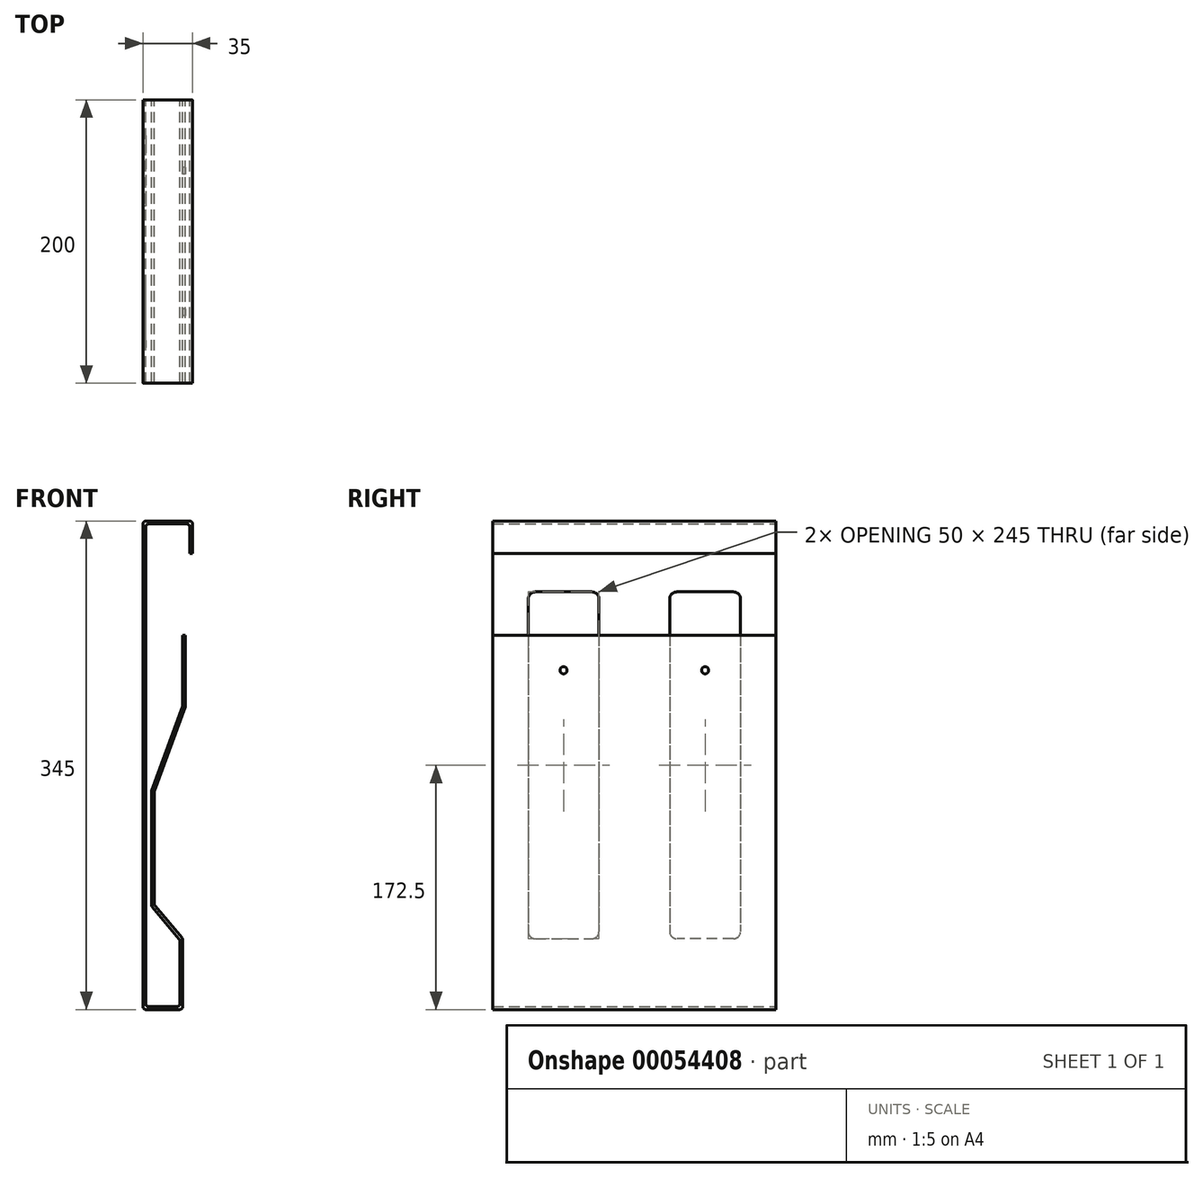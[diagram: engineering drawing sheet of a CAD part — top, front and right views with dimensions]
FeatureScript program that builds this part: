
annotation { "Feature Type Name" : "Feature", "Feature Type Description" : "" }
export const myFeature = defineFeature(function(context is Context, id is Id, definition is map)
    precondition{}
    {
        {
            var Q0;
            Q0=qCreatedBy(makeId("Front.planeOp"),FACE);
            var sketch = newSketch(context, id + "F0", { "sketchPlane" : qUnion([Q0])});
            skLineSegment(sketch, "E0", {"start": v(0, 0) * mm, "end": v(35, 0) * mm});
            skLineSegment(sketch, "E1", {"start": v(35, 0) * mm, "end": v(35, -23) * mm});
            skLineSegment(sketch, "E2", {"start": v(0, 0) * mm, "end": v(0, -345) * mm});
            skLineSegment(sketch, "E3", {"start": v(0, -345) * mm, "end": v(28, -345) * mm});
            skLineSegment(sketch, "E4", {"start": v(28, -295) * mm, "end": v(28, -345) * mm});
            skLineSegment(sketch, "E5.0", {"start": v(33, -2) * mm, "end": v(33, -23) * mm});
            skLineSegment(sketch, "E5.1", {"start": v(26, -295.73) * mm, "end": v(26, -343) * mm});
            skLineSegment(sketch, "E5.2", {"start": v(2, -343) * mm, "end": v(26, -343) * mm});
            skLineSegment(sketch, "E5.3", {"start": v(2, -2) * mm, "end": v(2, -343) * mm});
            skLineSegment(sketch, "E5.4", {"start": v(2, -2) * mm, "end": v(33, -2) * mm});
            skLineSegment(sketch, "E6", {"start": v(33, -23) * mm, "end": v(35, -23) * mm});
            skLineSegment(sketch, "E7", {"start": v(26, -295.73) * mm, "end": v(6, -271.9) * mm});
            skLineSegment(sketch, "E8", {"start": v(6, -271.9) * mm, "end": v(6, -190.81) * mm});
            skLineSegment(sketch, "E9", {"start": v(6, -190.81) * mm, "end": v(28, -130.37) * mm});
            skLineSegment(sketch, "E10", {"start": v(28, -130.37) * mm, "end": v(28, -80.72) * mm});
            skLineSegment(sketch, "E11.0", {"start": v(30, -130.72) * mm, "end": v(30, -80.72) * mm});
            skLineSegment(sketch, "E11.1", {"start": v(8, -191.16) * mm, "end": v(30, -130.72) * mm});
            skLineSegment(sketch, "E11.2", {"start": v(8, -271.16) * mm, "end": v(8, -191.16) * mm});
            skLineSegment(sketch, "E11.3", {"start": v(28, -295) * mm, "end": v(8, -271.16) * mm});
            skLineSegment(sketch, "E12", {"start": v(28, -80.72) * mm, "end": v(30, -80.72) * mm});
            skSolve(sketch);
        }
        {
            var Q0;
            Q0=qSketchRegion(id+"F0",true);
            extrude(context, id + "F1", {"entities" : qUnion([Q0]), "depth" : 200 * mm});
        }
        {
            var Q0;
            Q0=makeQuery(id+"F1.opExtrude","SWEPT_EDGE",EDGE,{"disambiguationData":[OSD([sQuery(id+"F0.wireOp",EDGE,"E0"),sQuery(id+"F0.wireOp",EDGE,"E2")])]});
            var Q1;
            Q1=makeQuery(id+"F1.opExtrude","SWEPT_EDGE",EDGE,{"disambiguationData":[OSD([sQuery(id+"F0.wireOp",EDGE,"E0"),sQuery(id+"F0.wireOp",EDGE,"E1")])]});
            var Q2;
            Q2=makeQuery(id+"F1.opExtrude","SWEPT_EDGE",EDGE,{"disambiguationData":[OSD([sQuery(id+"F0.wireOp",EDGE,"E5.0"),sQuery(id+"F0.wireOp",EDGE,"E5.4")])]});
            var Q3;
            Q3=makeQuery(id+"F1.opExtrude","SWEPT_EDGE",EDGE,{"disambiguationData":[OSD([sQuery(id+"F0.wireOp",EDGE,"E5.3"),sQuery(id+"F0.wireOp",EDGE,"E5.4")])]});
            var Q4;
            Q4=makeQuery(id+"F1.opExtrude","SWEPT_EDGE",EDGE,{"disambiguationData":[OSD([sQuery(id+"F0.wireOp",EDGE,"E2"),sQuery(id+"F0.wireOp",EDGE,"E3")])]});
            var Q5;
            Q5=makeQuery(id+"F1.opExtrude","SWEPT_EDGE",EDGE,{"disambiguationData":[OSD([sQuery(id+"F0.wireOp",EDGE,"E5.2"),sQuery(id+"F0.wireOp",EDGE,"E5.3")])]});
            var Q6;
            Q6=makeQuery(id+"F1.opExtrude","SWEPT_EDGE",EDGE,{"disambiguationData":[OSD([sQuery(id+"F0.wireOp",EDGE,"E3"),sQuery(id+"F0.wireOp",EDGE,"E4")])]});
            var Q7;
            Q7=makeQuery(id+"F1.opExtrude","SWEPT_EDGE",EDGE,{"disambiguationData":[OSD([sQuery(id+"F0.wireOp",EDGE,"E5.1"),sQuery(id+"F0.wireOp",EDGE,"E5.2")])]});
            var Q8;
            Q8=makeQuery(id+"F1.opExtrude","SWEPT_EDGE",EDGE,{"disambiguationData":[OSD([sQuery(id+"F0.wireOp",EDGE,"E5.1"),sQuery(id+"F0.wireOp",EDGE,"E7")])]});
            var Q9;
            Q9=makeQuery(id+"F1.opExtrude","SWEPT_EDGE",EDGE,{"disambiguationData":[OSD([sQuery(id+"F0.wireOp",EDGE,"E4"),sQuery(id+"F0.wireOp",EDGE,"E11.3")])]});
            var Q10;
            Q10=makeQuery(id+"F1.opExtrude","SWEPT_EDGE",EDGE,{"disambiguationData":[OSD([sQuery(id+"F0.wireOp",EDGE,"E11.2"),sQuery(id+"F0.wireOp",EDGE,"E11.3")])]});
            var Q11;
            Q11=makeQuery(id+"F1.opExtrude","SWEPT_EDGE",EDGE,{"disambiguationData":[OSD([sQuery(id+"F0.wireOp",EDGE,"E7"),sQuery(id+"F0.wireOp",EDGE,"E8")])]});
            var Q12;
            Q12=makeQuery(id+"F1.opExtrude","SWEPT_EDGE",EDGE,{"disambiguationData":[OSD([sQuery(id+"F0.wireOp",EDGE,"E8"),sQuery(id+"F0.wireOp",EDGE,"E9")])]});
            var Q13;
            Q13=makeQuery(id+"F1.opExtrude","SWEPT_EDGE",EDGE,{"disambiguationData":[OSD([sQuery(id+"F0.wireOp",EDGE,"E11.1"),sQuery(id+"F0.wireOp",EDGE,"E11.2")])]});
            var Q14;
            Q14=makeQuery(id+"F1.opExtrude","SWEPT_EDGE",EDGE,{"disambiguationData":[OSD([sQuery(id+"F0.wireOp",EDGE,"E11.0"),sQuery(id+"F0.wireOp",EDGE,"E11.1")])]});
            var Q15;
            Q15=makeQuery(id+"F1.opExtrude","SWEPT_EDGE",EDGE,{"disambiguationData":[OSD([sQuery(id+"F0.wireOp",EDGE,"E9"),sQuery(id+"F0.wireOp",EDGE,"E10")])]});
            fillet(context, id + "F2", {"entities" : qUnion([Q0, Q1, Q2, Q3, Q4, Q5, Q6, Q7, Q8, Q9, Q10, Q11, Q12, Q13, Q14, Q15]), "radius" : 2 * mm, "tangentPropagation" : true, "allowEdgeOverflow" : false});
        }
        {
            var Q0;
            Q0=makeQuery(id+"F1.opExtrude","SWEPT_FACE",FACE,{"disambiguationData":[OSD([sQuery(id+"F0.wireOp",EDGE,"E2")])]});
            var sketch = newSketch(context, id + "F3", { "sketchPlane" : qUnion([Q0])});
            skLineSegment(sketch, "E13", {"start": v(100, -2) * mm, "end": v(100, -30.01) * mm, "construction": true});
            skLineSegment(sketch, "E14.bottom", {"start": v(30, -50) * mm, "end": v(70, -50) * mm});
            skLineSegment(sketch, "E14.top", {"start": v(30, -295) * mm, "end": v(70, -295) * mm});
            skLineSegment(sketch, "E14.left", {"start": v(25, -55) * mm, "end": v(25, -290) * mm});
            skLineSegment(sketch, "E14.right", {"start": v(75, -55) * mm, "end": v(75, -290) * mm});
            skPoint(sketch, "E15.visualSharp", {"position": v(25, -50) * mm});
            skArc(sketch, "E15.filletArc", {"start": v(30, -50) * mm, "mid": v(26.46, -51.46) * mm, "end": v(25, -55) * mm});
            skPoint(sketch, "E16.visualSharp", {"position": v(75, -295) * mm});
            skArc(sketch, "E16.filletArc", {"start": v(70, -295) * mm, "mid": v(73.54, -293.54) * mm, "end": v(75, -290) * mm});
            skPoint(sketch, "E17.visualSharp", {"position": v(25, -295) * mm});
            skArc(sketch, "E17.filletArc", {"start": v(25, -290) * mm, "mid": v(26.46, -293.54) * mm, "end": v(30, -295) * mm});
            skPoint(sketch, "E18.visualSharp", {"position": v(75, -50) * mm});
            skArc(sketch, "E18.filletArc", {"start": v(75, -55) * mm, "mid": v(73.54, -51.46) * mm, "end": v(70, -50) * mm});
            skArc(sketch, "E19.MirrorCS", {"start": v(125, -55) * mm, "mid": v(126.46, -51.46) * mm, "end": v(130, -50) * mm});
            skArc(sketch, "E20.MirrorCS", {"start": v(175, -290) * mm, "mid": v(173.54, -293.54) * mm, "end": v(170, -295) * mm});
            skArc(sketch, "E21.MirrorCS", {"start": v(170, -50) * mm, "mid": v(173.54, -51.46) * mm, "end": v(175, -55) * mm});
            skArc(sketch, "E22.MirrorCS", {"start": v(130, -295) * mm, "mid": v(126.46, -293.54) * mm, "end": v(125, -290) * mm});
            skPoint(sketch, "E23.MirrorP", {"position": v(125, -50) * mm});
            skLineSegment(sketch, "E24.MirrorCS", {"start": v(170, -50) * mm, "end": v(130, -50) * mm});
            skPoint(sketch, "E25.MirrorP", {"position": v(175, -295) * mm});
            skLineSegment(sketch, "E26.MirrorCS", {"start": v(170, -295) * mm, "end": v(130, -295) * mm});
            skLineSegment(sketch, "E27.MirrorCS", {"start": v(175, -55) * mm, "end": v(175, -290) * mm});
            skPoint(sketch, "E28.MirrorP", {"position": v(175, -50) * mm});
            skLineSegment(sketch, "E29.MirrorCS", {"start": v(125, -55) * mm, "end": v(125, -290) * mm});
            skPoint(sketch, "E30.MirrorP", {"position": v(125, -295) * mm});
            skSolve(sketch);
        }
        {
            var Q0;
            Q0 = qSketchRegion(id + "F3", true);
            extrude(context, id + "F4", {"entities" : qUnion([Q0]), "operationType" : NewBodyOperationType.REMOVE, "oppositeDirection" : true, "depth" : 2 * mm});
        }
        {
            var Q0;
            Q0=makeQuery(id+"F1.opExtrude","SWEPT_FACE",FACE,{"disambiguationData":[OSD([sQuery(id+"F0.wireOp",EDGE,"E10")])]});
            var sketch = newSketch(context, id + "F5", { "sketchPlane" : qUnion([Q0])});
            skLineSegment(sketch, "E31", {"start": v(0, -105.37) * mm, "end": v(200, -105.37) * mm, "construction": true});
            skPoint(sketch, "E32", {"position": v(50, -105.37) * mm});
            skPoint(sketch, "E33", {"position": v(150, -105.37) * mm});
            skSolve(sketch);
        }
        {
            var Q0;
            Q0=sQuery(id+"F5.wireOp",VERTEX,"E32");
            var Q1;
            Q1=sQuery(id+"F5.wireOp",VERTEX,"E33");
            var Q2;
            Q2=makeQuery(id+"F1.opExtrude","SWEPT_BODY",BODY,{"disambiguationData":[OSD([sQuery(id+"F0.wireOp",EDGE,"E0"),sQuery(id+"F0.wireOp",EDGE,"E1"),sQuery(id+"F0.wireOp",EDGE,"E2"),sQuery(id+"F0.wireOp",EDGE,"E3"),sQuery(id+"F0.wireOp",EDGE,"E4"),sQuery(id+"F0.wireOp",EDGE,"E5.0"),sQuery(id+"F0.wireOp",EDGE,"E5.1"),sQuery(id+"F0.wireOp",EDGE,"E5.2"),sQuery(id+"F0.wireOp",EDGE,"E5.3"),sQuery(id+"F0.wireOp",EDGE,"E5.4"),sQuery(id+"F0.wireOp",EDGE,"E6"),sQuery(id+"F0.wireOp",EDGE,"E7"),sQuery(id+"F0.wireOp",EDGE,"E8"),sQuery(id+"F0.wireOp",EDGE,"E9"),sQuery(id+"F0.wireOp",EDGE,"E10"),sQuery(id+"F0.wireOp",EDGE,"E11.0"),sQuery(id+"F0.wireOp",EDGE,"E11.1"),sQuery(id+"F0.wireOp",EDGE,"E11.2"),sQuery(id+"F0.wireOp",EDGE,"E11.3"),sQuery(id+"F0.wireOp",EDGE,"E12")])]});
            hole(context, id + "F6", {"style" : HoleStyle.SIMPLE, "endStyle" : HoleEndStyle.BLIND, "holeDiameter" : 5 * mm, "holeDepth" : 2 * mm, "locations" : qUnion([Q0, Q1]), "scope" : qUnion([Q2])});
        }
    });
